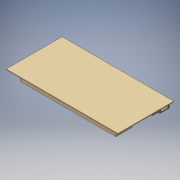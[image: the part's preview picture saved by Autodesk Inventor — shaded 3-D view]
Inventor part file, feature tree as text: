
AUTODESK INVENTOR PART (.ipt)
format: ipt  version: 2018 (Build 220112000, 112)  size: 241,664 bytes
history: native  units: in
note: dims shown in document units (in); Inventor stores cm internally (conversion verified against a paired STEP export)
features: sketch x9, extrude x8, pattern_linear x1
ambient origin geometry x8: Origin, YZ Plane, XZ Plane, XY Plane, X Axis, Y Axis, Z Axis, Center Point
bodies: Solid1 (feature_tree)
feature tree (18):
  extrude  "Extrusion1"  Depth=120.0in
  pattern_linear  "Rectangular Pattern1"  Count1=6 Spacing1=240.0in
  extrude  "Extrusion4"  Depth=100.0in TaperAngle=0.0deg
  sketch  "Sketch5"  dims[d26=100.0in d27=0.0in d28=100.0in d29=0.0in]
  extrude  "Extrusion5"  Depth=200.0in TaperAngle=0.0deg
  extrude  "Extrusion6"  Depth=50.0in TaperAngle=0.0deg
  extrude  "Extrusion7"  [1 undecoded]
  extrude  "Extrusion8"  [1 undecoded]
  extrude  "Extrusion9"  [1 undecoded]
  extrude  "Extrusion10"  [1 undecoded]
  sketch  "Sketch11"
  sketch  "Sketch1"  dims[d0=240.0in d1=120.0in]
  sketch  "Sketch4"  dims[d2=10.0in d3=0.0in d4=2.3622in d6=240.0in d7=2.3622in d9=120.0in]
  sketch  "Sketch6"  dims[d30=200.0in d31=0.0in d32=200.0in d33=0.0in]
  sketch  "Sketch7"  dims[d34=50.0in d35=0.0in d36=50.0in d37=0.0in]
  sketch  "Sketch8"  dims[d38=50.0in d39=0.0in]
  sketch  "Sketch9"
  sketch  "Sketch10"
note: 4 required parameter values undecoded (feature->parameter linkage not recoverable at this tier; creation-order binding heuristic only, values carry confidence <= 0.55)
